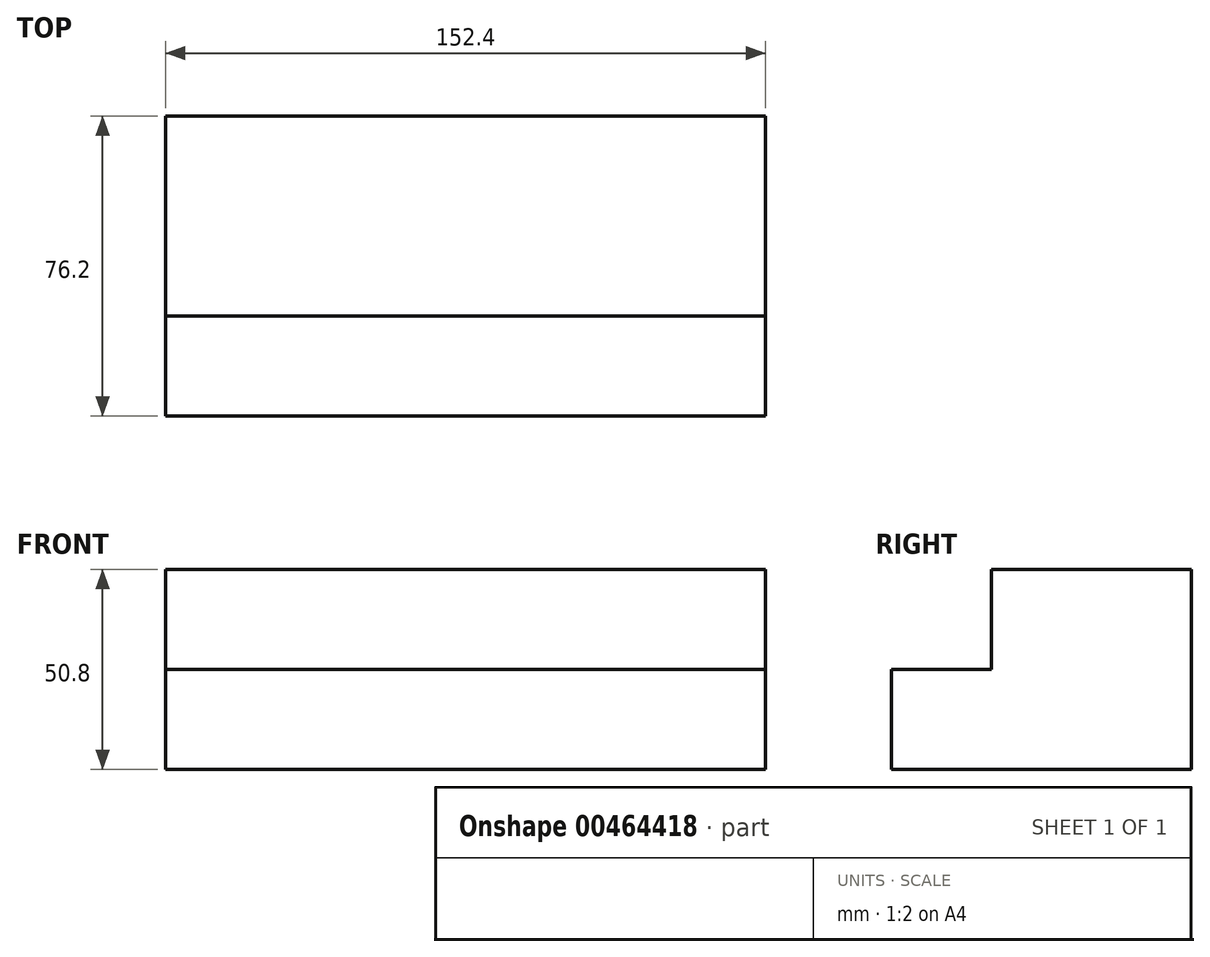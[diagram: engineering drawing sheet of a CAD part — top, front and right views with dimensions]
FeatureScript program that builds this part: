
annotation { "Feature Type Name" : "Feature", "Feature Type Description" : "" }
export const myFeature = defineFeature(function(context is Context, id is Id, definition is map)
    precondition{}
    {
        {
            var Q0;
            Q0=qCreatedBy(makeId("Right.planeOp"),FACE);
            var sketch = newSketch(context, id + "F0", { "sketchPlane" : qUnion([Q0])});
            skLineSegment(sketch, "E0", {"start": v(72.24, 66.4) * mm, "end": v(21.44, 66.4) * mm});
            skLineSegment(sketch, "E1", {"start": v(21.44, 66.4) * mm, "end": v(21.44, 41) * mm});
            skLineSegment(sketch, "E2", {"start": v(21.44, 41) * mm, "end": v(-3.96, 41) * mm});
            skLineSegment(sketch, "E3", {"start": v(-3.96, 41) * mm, "end": v(-3.96, 15.6) * mm});
            skLineSegment(sketch, "E4", {"start": v(-3.96, 15.6) * mm, "end": v(72.24, 15.6) * mm});
            skLineSegment(sketch, "E5", {"start": v(72.24, 15.6) * mm, "end": v(72.24, 66.4) * mm});
            skSolve(sketch);
        }
        {
            var Q0;
            Q0=makeQuery(id+"F0.imprint","IMPRINT",FACE,{"disambiguationData":[TD([[makeQuery(id+"F0.imprint","IMPRINT",EDGE,{"derivedFrom":sQuery(id+"F0.wireOp",EDGE,"E0")}),1.0]])]});
            extrude(context, id + "F1", {"entities" : qUnion([Q0]), "depth" : 152.4 * mm});
        }
    });
